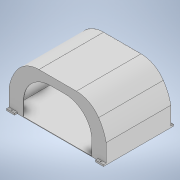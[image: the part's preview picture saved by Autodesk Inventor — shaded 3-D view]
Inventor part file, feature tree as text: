
AUTODESK INVENTOR PART (.ipt)
format: ipt  version: 2021 (Build 250183000, 183)  size: 203,776 bytes
history: native  units: mm
features: extrude x6, sketch x6, mirror x2, fillet x2, shell x1, plane x1
ambient origin geometry x8: Origin, YZ Plane, XZ Plane, XY Plane, X Axis, Y Axis, Z Axis, Center Point
bodies: Solid1 (feature_tree)
feature tree (18):
  extrude  "Extrusion1"  Depth=1800.0mm
  extrude  "Extrusion2"  Depth=900.0mm
  mirror  "Mirror1"
  fillet  "Fillet1"  Radius=550.0mm
  sketch  "Sketch3"  dims[d8=1200.0mm d9=0.0mm d10=500.0mm]
  shell  "Shell2"  Thickness=350.0mm
  extrude  "Extrusion3"  TaperAngle=0.0deg  [1 undecoded]
  fillet  "Fillet2"  Radius=500.0mm
  extrude  "Extrusion4"  Depth=150.0mm
  extrude  "Extrusion5"  Depth=10.0mm TaperAngle=0.0deg
  extrude  "Extrusion6"  Depth=10.0mm TaperAngle=0.0deg
  mirror  "Mirror2"
  sketch  "Sketch1"  dims[d0=900.0mm d1=1800.0mm]
  sketch  "Sketch2"  dims[d2=1200.0mm d3=0.0mm d5=900.0mm d6=550.0mm d7=350.0mm]
  plane  "Work Plane1"
  sketch  "Sketch4"  dims[d11=150.0mm d12=600.0mm]
  sketch  "Sketch5"  dims[d13=5.0mm d14=10.0mm d15=0.0mm]
  sketch  "Sketch6"  dims[d16=500.0mm d17=10.0mm d18=0.0mm d19=30.0mm d20=150.0mm d21=30.0mm d22=150.0mm d23=50.0mm d24=0.0mm d25=16.0mm d26=25.0mm d27=75.0mm d28=75.0mm d29=50.0mm d30=0.0mm d31=0.5mm d32=0.872665mm d33=0.5mm d34=0.872665mm]
note: 1 required parameter value undecoded (feature->parameter linkage not recoverable at this tier; creation-order binding heuristic only, values carry confidence <= 0.55)
